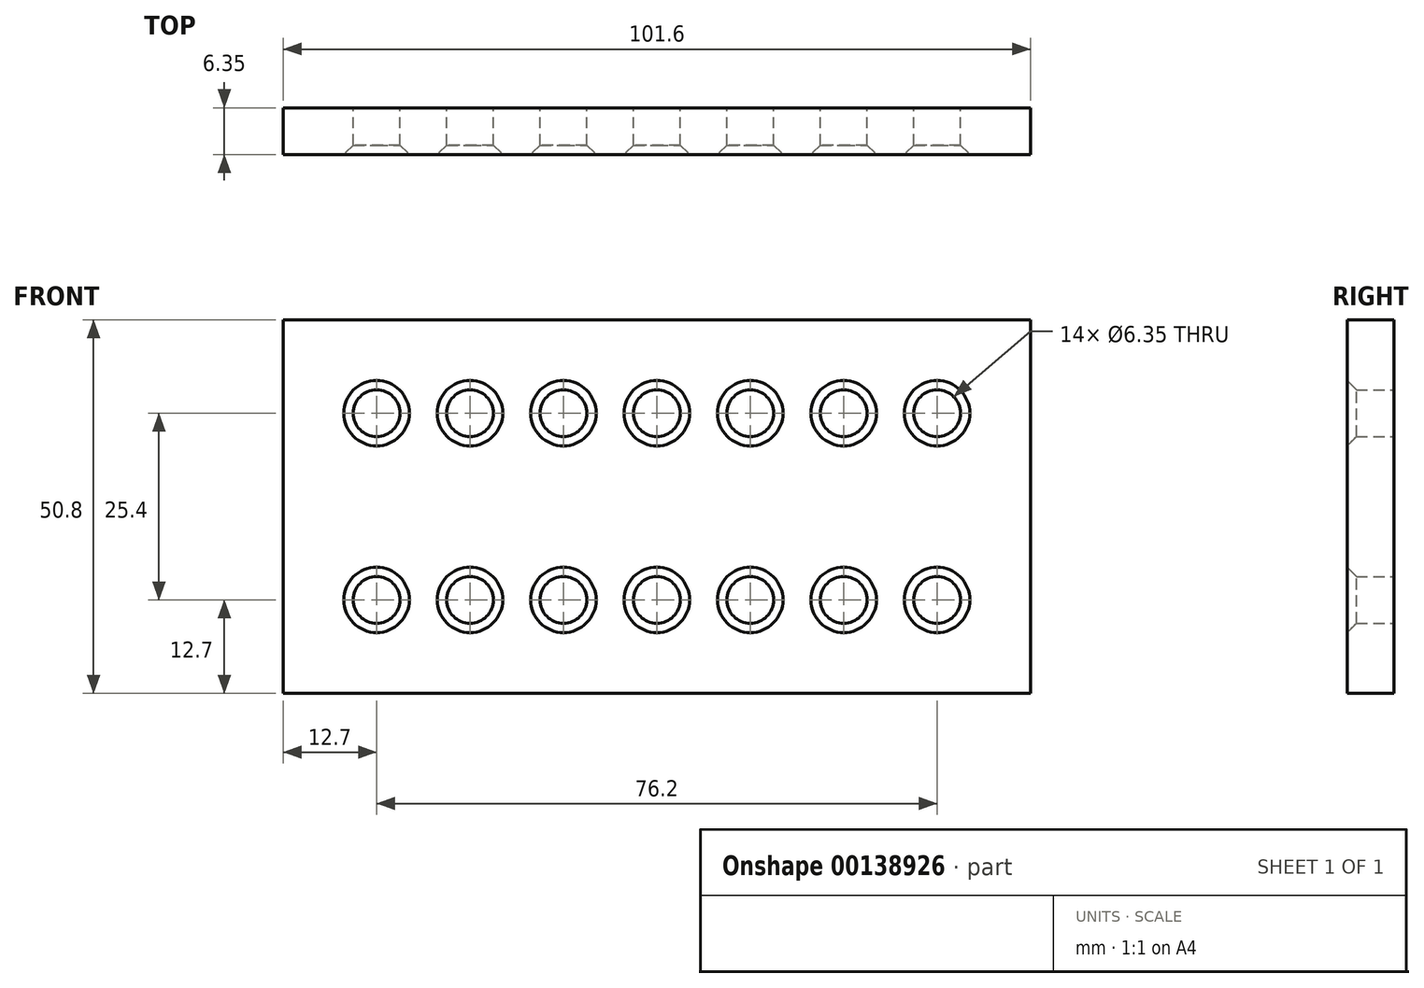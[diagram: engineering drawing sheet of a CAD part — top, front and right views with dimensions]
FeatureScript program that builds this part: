
annotation { "Feature Type Name" : "Feature", "Feature Type Description" : "" }
export const myFeature = defineFeature(function(context is Context, id is Id, definition is map)
    precondition{}
    {
        {
            var Q0;
            Q0=qCreatedBy(makeId("Front.planeOp"),FACE);
            var sketch = newSketch(context, id + "F0", { "sketchPlane" : qUnion([Q0])});
            skLineSegment(sketch, "E0.bottom", {"start": v(-50.8, 25.4) * mm, "end": v(50.8, 25.4) * mm});
            skLineSegment(sketch, "E0.top", {"start": v(-50.8, -25.4) * mm, "end": v(50.8, -25.4) * mm});
            skLineSegment(sketch, "E0.left", {"start": v(-50.8, 25.4) * mm, "end": v(-50.8, -25.4) * mm});
            skLineSegment(sketch, "E0.right", {"start": v(50.8, 25.4) * mm, "end": v(50.8, -25.4) * mm});
            skPoint(sketch, "E0.middle", {"position": v(0, 0) * mm});
            skCircle(sketch, "E1", {"center": v(-38.1, 12.7) * mm, "radius": 3.18 * mm});
            skCircle(sketch, "E2.0.1.0", {"center": v(-38.1, -12.7) * mm, "radius": 3.18 * mm});
            skCircle(sketch, "E2.1.0.0", {"center": v(-25.4, 12.7) * mm, "radius": 3.18 * mm});
            skCircle(sketch, "E2.1.1.0", {"center": v(-25.4, -12.7) * mm, "radius": 3.18 * mm});
            skCircle(sketch, "E2.2.0.0", {"center": v(-12.7, 12.7) * mm, "radius": 3.18 * mm});
            skCircle(sketch, "E2.2.1.0", {"center": v(-12.7, -12.7) * mm, "radius": 3.18 * mm});
            skCircle(sketch, "E2.3.0.0", {"center": v(0, 12.7) * mm, "radius": 3.18 * mm});
            skCircle(sketch, "E2.3.1.0", {"center": v(0, -12.7) * mm, "radius": 3.18 * mm});
            skCircle(sketch, "E2.4.0.0", {"center": v(12.7, 12.7) * mm, "radius": 3.18 * mm});
            skCircle(sketch, "E2.4.1.0", {"center": v(12.7, -12.7) * mm, "radius": 3.18 * mm});
            skCircle(sketch, "E2.5.0.0", {"center": v(25.4, 12.7) * mm, "radius": 3.18 * mm});
            skCircle(sketch, "E2.5.1.0", {"center": v(25.4, -12.7) * mm, "radius": 3.18 * mm});
            skCircle(sketch, "E2.6.0.0", {"center": v(38.1, 12.7) * mm, "radius": 3.18 * mm});
            skCircle(sketch, "E2.6.1.0", {"center": v(38.1, -12.7) * mm, "radius": 3.18 * mm});
            skLineSegment(sketch, "E2.direction1", {"start": v(-38.1, 12.7) * mm, "end": v(-25.4, 12.7) * mm, "construction": true});
            skLineSegment(sketch, "E2.direction2", {"start": v(-38.1, 12.7) * mm, "end": v(-38.1, -12.7) * mm, "construction": true});
            skSolve(sketch);
        }
        {
            var Q0;
            Q0=makeQuery(id+"F0.imprint","IMPRINT",FACE,{"disambiguationData":[TD([[makeQuery(id+"F0.imprint","IMPRINT",EDGE,{"derivedFrom":sQuery(id+"F0.wireOp",EDGE,"E0.bottom")}),-1.0]])]});
            extrude(context, id + "F1", {"entities" : qUnion([Q0]), "depth" : 6.35 * mm});
        }
        {
            var Q0;
            Q0=makeQuery(id+"F1.opExtrude","CAP_EDGE",EDGE,{"disambiguationData":[OSD([sQuery(id+"F0.wireOp",EDGE,"E1")])],"isStart":false});
            var Q1;
            Q1=makeQuery(id+"F1.opExtrude","CAP_EDGE",EDGE,{"disambiguationData":[OSD([sQuery(id+"F0.wireOp",EDGE,"E2.1.0.0")])],"isStart":false});
            var Q2;
            Q2=makeQuery(id+"F1.opExtrude","CAP_EDGE",EDGE,{"disambiguationData":[OSD([sQuery(id+"F0.wireOp",EDGE,"E2.2.0.0")])],"isStart":false});
            var Q3;
            Q3=makeQuery(id+"F1.opExtrude","CAP_EDGE",EDGE,{"disambiguationData":[OSD([sQuery(id+"F0.wireOp",EDGE,"E2.3.0.0")])],"isStart":false});
            var Q4;
            Q4=makeQuery(id+"F1.opExtrude","CAP_EDGE",EDGE,{"disambiguationData":[OSD([sQuery(id+"F0.wireOp",EDGE,"E2.4.0.0")])],"isStart":false});
            var Q5;
            Q5=makeQuery(id+"F1.opExtrude","CAP_EDGE",EDGE,{"disambiguationData":[OSD([sQuery(id+"F0.wireOp",EDGE,"E2.5.0.0")])],"isStart":false});
            var Q6;
            Q6=makeQuery(id+"F1.opExtrude","CAP_EDGE",EDGE,{"disambiguationData":[OSD([sQuery(id+"F0.wireOp",EDGE,"E2.6.0.0")])],"isStart":false});
            var Q7;
            Q7=makeQuery(id+"F1.opExtrude","CAP_EDGE",EDGE,{"disambiguationData":[OSD([sQuery(id+"F0.wireOp",EDGE,"E2.6.1.0")])],"isStart":false});
            var Q8;
            Q8=makeQuery(id+"F1.opExtrude","CAP_EDGE",EDGE,{"disambiguationData":[OSD([sQuery(id+"F0.wireOp",EDGE,"E2.5.1.0")])],"isStart":false});
            var Q9;
            Q9=makeQuery(id+"F1.opExtrude","CAP_EDGE",EDGE,{"disambiguationData":[OSD([sQuery(id+"F0.wireOp",EDGE,"E2.4.1.0")])],"isStart":false});
            var Q10;
            Q10=makeQuery(id+"F1.opExtrude","CAP_EDGE",EDGE,{"disambiguationData":[OSD([sQuery(id+"F0.wireOp",EDGE,"E2.3.1.0")])],"isStart":false});
            var Q11;
            Q11=makeQuery(id+"F1.opExtrude","CAP_EDGE",EDGE,{"disambiguationData":[OSD([sQuery(id+"F0.wireOp",EDGE,"E2.2.1.0")])],"isStart":false});
            var Q12;
            Q12=makeQuery(id+"F1.opExtrude","CAP_EDGE",EDGE,{"disambiguationData":[OSD([sQuery(id+"F0.wireOp",EDGE,"E2.0.1.0")])],"isStart":false});
            var Q13;
            Q13=makeQuery(id+"F1.opExtrude","CAP_EDGE",EDGE,{"disambiguationData":[OSD([sQuery(id+"F0.wireOp",EDGE,"E2.1.1.0")])],"isStart":false});
            chamfer(context, id + "F2", {"entities" : qUnion([Q0, Q1, Q2, Q3, Q4, Q5, Q6, Q7, Q8, Q9, Q10, Q11, Q12, Q13]), "width" : 1.27 * mm, "tangentPropagation" : true});
        }
    });
